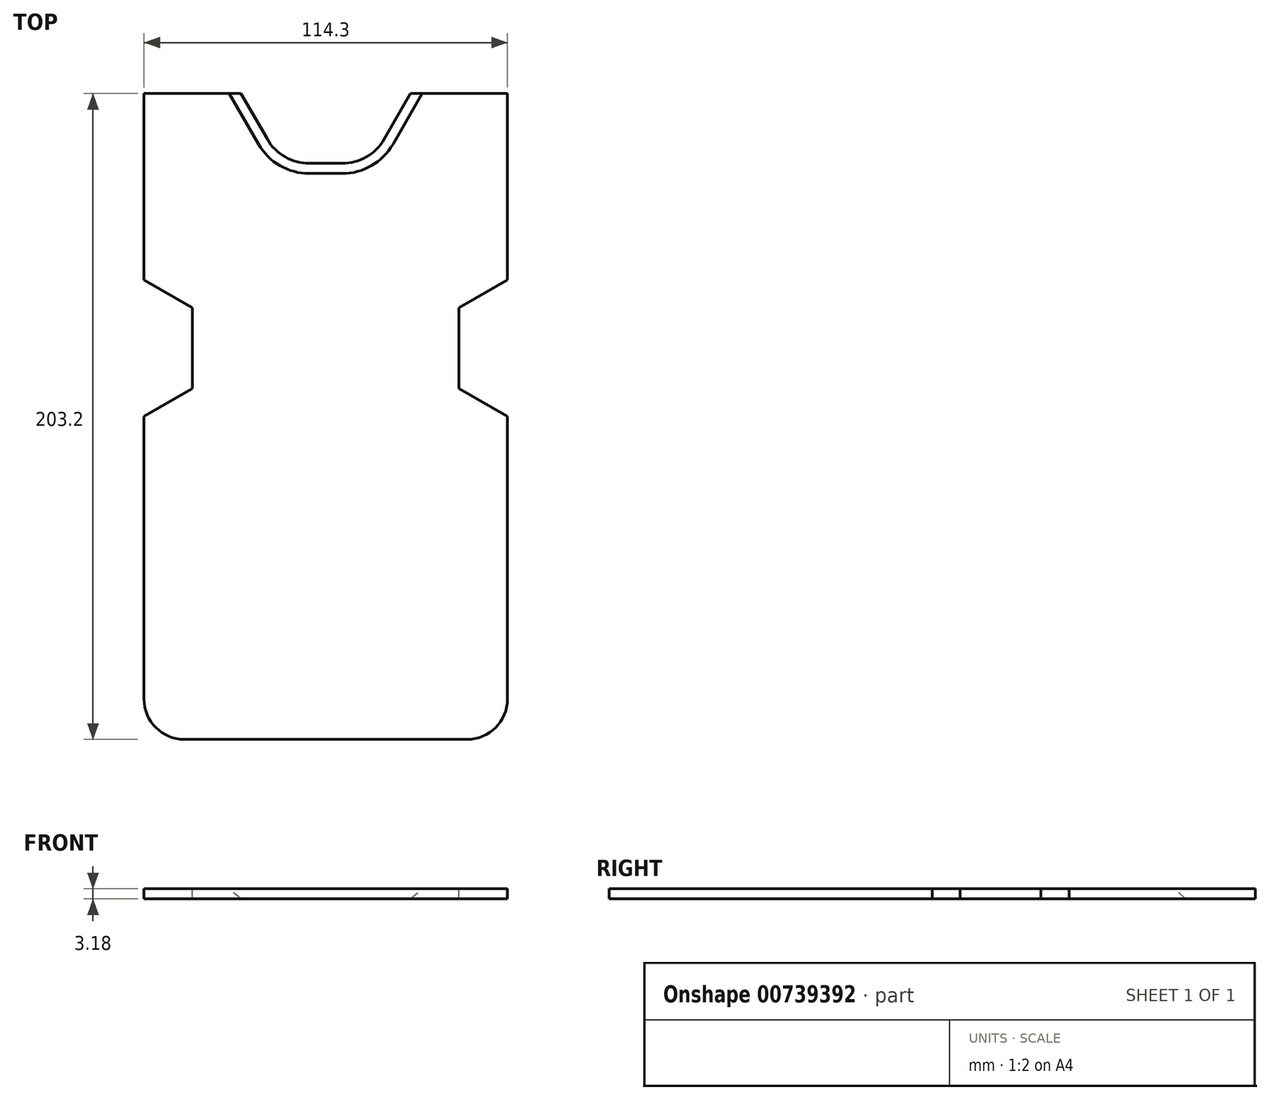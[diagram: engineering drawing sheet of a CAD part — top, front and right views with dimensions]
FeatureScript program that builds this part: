
annotation { "Feature Type Name" : "Feature", "Feature Type Description" : "" }
export const myFeature = defineFeature(function(context is Context, id is Id, definition is map)
    precondition{}
    {
        {
            var Q0;
            Q0=qCreatedBy(makeId("Top.planeOp"),FACE);
            var sketch = newSketch(context, id + "F0", { "sketchPlane" : qUnion([Q0])});
            skLineSegment(sketch, "E0.bottom", {"start": v(-57.15, -25.4) * mm, "end": v(57.15, -25.4) * mm});
            skLineSegment(sketch, "E0.top", {"start": v(-57.15, 25.4) * mm, "end": v(57.15, 25.4) * mm});
            skLineSegment(sketch, "E0.left", {"start": v(-57.15, -25.4) * mm, "end": v(-57.15, 25.4) * mm});
            skLineSegment(sketch, "E0.right", {"start": v(57.15, -25.4) * mm, "end": v(57.15, 25.4) * mm});
            skLineSegment(sketch, "E1", {"start": v(57.15, -25.4) * mm, "end": v(-57.15, 25.4) * mm, "construction": true});
            skLineSegment(sketch, "E2", {"start": v(57.15, 25.4) * mm, "end": v(-57.15, -25.4) * mm, "construction": true});
            skPoint(sketch, "E3", {"position": v(0, 0) * mm});
            skSolve(sketch);
        }
        {
            var Q0;
            Q0=makeQuery(id+"F0.imprint","IMPRINT",FACE,{"disambiguationData":[TD([[makeQuery(id+"F0.imprint","IMPRINT",EDGE,{"derivedFrom":sQuery(id+"F0.wireOp",EDGE,"E0.bottom")}),1.0]])]});
            extrude(context, id + "F1", {"entities" : qUnion([Q0]), "depth" : 3.17 * mm, "offsetDistance" : 25.4 * mm});
        }
        {
            var Q0;
            Q0=makeQuery(id+"F1.opExtrude","SWEPT_FACE",FACE,{"disambiguationData":[OSD([sQuery(id+"F0.wireOp",EDGE,"E0.top")])]});
            extrude(context, id + "F2", {"entities" : qUnion([Q0]), "operationType" : NewBodyOperationType.ADD, "depth" : 152.4 * mm, "offsetDistance" : 25.4 * mm});
        }
        {
            var Q0;
            {var subQ0=sQuery(id+"F0.wireOp",EDGE,"E0.top");Q0=makeQuery(id+"F2.boolean.opBoolean","MERGE",FACE,{"derivedFrom":[makeQuery(id+"F1.opExtrude","CAP_FACE",FACE,{"disambiguationData":[OSD([sQuery(id+"F0.wireOp",EDGE,"E0.bottom"),subQ0,sQuery(id+"F0.wireOp",EDGE,"E0.left"),sQuery(id+"F0.wireOp",EDGE,"E0.right")])],"isStart":false}),makeQuery(id+"F2.opExtrude","SWEPT_FACE",FACE,{"disambiguationData":[OSD([subQ0]),TDD([makeQuery(id+"F1.opExtrude","CAP_EDGE",EDGE,{"disambiguationData":[OSD([subQ0])],"isStart":false})])]})]});}
            var sketch = newSketch(context, id + "F3", { "sketchPlane" : qUnion([Q0])});
            skLineSegment(sketch, "E4", {"start": v(13.97, 155.8) * mm, "end": v(-13.97, 155.8) * mm});
            skLineSegment(sketch, "E5", {"start": v(-13.97, 155.8) * mm, "end": v(-26.67, 177.8) * mm});
            skLineSegment(sketch, "E6", {"start": v(13.97, 155.8) * mm, "end": v(26.67, 177.8) * mm});
            skLineSegment(sketch, "E7", {"start": v(0, 155.8) * mm, "end": v(0, 177.8) * mm, "construction": true});
            skLineSegment(sketch, "E8", {"start": v(-57.15, 76.2) * mm, "end": v(-41.91, 85) * mm});
            skLineSegment(sketch, "E9", {"start": v(-41.91, 85) * mm, "end": v(-41.91, 110.4) * mm});
            skLineSegment(sketch, "E10", {"start": v(-41.9, 110.4) * mm, "end": v(-57.15, 119.2) * mm});
            skLineSegment(sketch, "E11", {"start": v(57.15, 76.2) * mm, "end": v(41.91, 85) * mm});
            skLineSegment(sketch, "E12", {"start": v(41.91, 85) * mm, "end": v(41.91, 110.4) * mm});
            skLineSegment(sketch, "E13", {"start": v(41.91, 110.4) * mm, "end": v(57.15, 119.2) * mm});
            skSolve(sketch);
        }
        {
            var Q0;
            Q0=makeQuery(id+"F3.imprint","IMPRINT",FACE,{"disambiguationData":[TD([[makeQuery(id+"F3.imprint","IMPRINT",EDGE,{"derivedFrom":sQuery(id+"F3.wireOp",EDGE,"E4")}),-1.0]])]});
            extrude(context, id + "F4", {"entities" : qUnion([Q0]), "operationType" : NewBodyOperationType.REMOVE, "oppositeDirection" : true, "depth" : 3.3 * mm, "offsetDistance" : 25.4 * mm});
        }
        {
            var Q0;
            Q0=makeQuery(id+"F4.boolean.opBoolean","COPY",EDGE,{"derivedFrom":makeQuery(id+"F4.opExtrude","SWEPT_EDGE",EDGE,{"disambiguationData":[OSD([sQuery(id+"F3.wireOp",EDGE,"E4"),sQuery(id+"F3.wireOp",EDGE,"E6")])]})});
            var Q1;
            Q1=makeQuery(id+"F4.boolean.opBoolean","COPY",EDGE,{"derivedFrom":makeQuery(id+"F4.opExtrude","SWEPT_EDGE",EDGE,{"disambiguationData":[OSD([sQuery(id+"F3.wireOp",EDGE,"E4"),sQuery(id+"F3.wireOp",EDGE,"E5")])]})});
            fillet(context, id + "F5", {"entities" : qUnion([Q0, Q1]), "radius" : 15.24 * mm, "tangentPropagation" : true, "allowEdgeOverflow" : false});
        }
        {
            var Q0;
            Q0=makeQuery(id+"F1.opExtrude","SWEPT_EDGE",EDGE,{"disambiguationData":[OSD([sQuery(id+"F0.wireOp",EDGE,"E0.bottom"),sQuery(id+"F0.wireOp",EDGE,"E0.right")])]});
            var Q1;
            Q1=makeQuery(id+"F1.opExtrude","SWEPT_EDGE",EDGE,{"disambiguationData":[OSD([sQuery(id+"F0.wireOp",EDGE,"E0.bottom"),sQuery(id+"F0.wireOp",EDGE,"E0.left")])]});
            fillet(context, id + "F6", {"entities" : qUnion([Q0, Q1]), "radius" : 12.7 * mm, "tangentPropagation" : true, "allowEdgeOverflow" : false});
        }
        {
            var Q0;
            {var subQ0=sQuery(id+"F3.wireOp",EDGE,"E11");Q0=makeQuery(id+"F3.imprint","IMPRINT",FACE,{"disambiguationData":[TD([[makeQuery(id+"F3.imprint","IMPRINT",EDGE,{"derivedFrom":subQ0}),-1.0]])]});}
            var Q1;
            {var subQ0=sQuery(id+"F3.wireOp",EDGE,"E8");Q1=makeQuery(id+"F3.imprint","IMPRINT",FACE,{"disambiguationData":[TD([[makeQuery(id+"F3.imprint","IMPRINT",EDGE,{"derivedFrom":subQ0}),1.0]])]});}
            extrude(context, id + "F7", {"entities" : qUnion([Q0, Q1]), "operationType" : NewBodyOperationType.REMOVE, "oppositeDirection" : true, "depth" : 3.17 * mm, "offsetDistance" : 25.4 * mm});
        }
        {
            var Q0;
            Q0=makeQuery(id+"F4.boolean.opBoolean","COPY",EDGE,{"derivedFrom":makeQuery(id+"F4.opExtrude","CAP_EDGE",EDGE,{"disambiguationData":[OSD([sQuery(id+"F3.wireOp",EDGE,"E5")])],"isStart":true})});
            var Q1;
            {var subQ0=sQuery(id+"F0.wireOp",EDGE,"E0.top");Q1=makeQuery(id+"F5.opFillet","BLEND_EDGE",EDGE,{"blendedFrom":[makeQuery(id+"F4.boolean.opBoolean","COPY",EDGE,{"derivedFrom":makeQuery(id+"F4.opExtrude","SWEPT_EDGE",EDGE,{"disambiguationData":[OSD([sQuery(id+"F3.wireOp",EDGE,"E4"),sQuery(id+"F3.wireOp",EDGE,"E5")])]})}),makeQuery(id+"F2.boolean.opBoolean","MERGE",FACE,{"derivedFrom":[makeQuery(id+"F1.opExtrude","CAP_FACE",FACE,{"disambiguationData":[OSD([sQuery(id+"F0.wireOp",EDGE,"E0.bottom"),subQ0,sQuery(id+"F0.wireOp",EDGE,"E0.left"),sQuery(id+"F0.wireOp",EDGE,"E0.right")])],"isStart":false}),makeQuery(id+"F2.opExtrude","SWEPT_FACE",FACE,{"disambiguationData":[OSD([subQ0]),TDD([makeQuery(id+"F1.opExtrude","CAP_EDGE",EDGE,{"disambiguationData":[OSD([subQ0])],"isStart":false})])]})]})],"blendedInto":[makeQuery(id+"F2.boolean.opBoolean","MERGE",FACE,{"derivedFrom":[makeQuery(id+"F1.opExtrude","CAP_FACE",FACE,{"disambiguationData":[OSD([sQuery(id+"F0.wireOp",EDGE,"E0.bottom"),subQ0,sQuery(id+"F0.wireOp",EDGE,"E0.left"),sQuery(id+"F0.wireOp",EDGE,"E0.right")])],"isStart":false}),makeQuery(id+"F2.opExtrude","SWEPT_FACE",FACE,{"disambiguationData":[OSD([subQ0]),TDD([makeQuery(id+"F1.opExtrude","CAP_EDGE",EDGE,{"disambiguationData":[OSD([subQ0])],"isStart":false})])]})]})]});}
            var Q2;
            Q2=makeQuery(id+"F4.boolean.opBoolean","COPY",EDGE,{"derivedFrom":makeQuery(id+"F4.opExtrude","CAP_EDGE",EDGE,{"disambiguationData":[OSD([sQuery(id+"F3.wireOp",EDGE,"E4")])],"isStart":true})});
            var Q3;
            {var subQ0=sQuery(id+"F0.wireOp",EDGE,"E0.top");Q3=makeQuery(id+"F5.opFillet","BLEND_EDGE",EDGE,{"blendedFrom":[makeQuery(id+"F4.boolean.opBoolean","COPY",EDGE,{"derivedFrom":makeQuery(id+"F4.opExtrude","SWEPT_EDGE",EDGE,{"disambiguationData":[OSD([sQuery(id+"F3.wireOp",EDGE,"E4"),sQuery(id+"F3.wireOp",EDGE,"E6")])]})}),makeQuery(id+"F2.boolean.opBoolean","MERGE",FACE,{"derivedFrom":[makeQuery(id+"F1.opExtrude","CAP_FACE",FACE,{"disambiguationData":[OSD([sQuery(id+"F0.wireOp",EDGE,"E0.bottom"),subQ0,sQuery(id+"F0.wireOp",EDGE,"E0.left"),sQuery(id+"F0.wireOp",EDGE,"E0.right")])],"isStart":false}),makeQuery(id+"F2.opExtrude","SWEPT_FACE",FACE,{"disambiguationData":[OSD([subQ0]),TDD([makeQuery(id+"F1.opExtrude","CAP_EDGE",EDGE,{"disambiguationData":[OSD([subQ0])],"isStart":false})])]})]})],"blendedInto":[makeQuery(id+"F2.boolean.opBoolean","MERGE",FACE,{"derivedFrom":[makeQuery(id+"F1.opExtrude","CAP_FACE",FACE,{"disambiguationData":[OSD([sQuery(id+"F0.wireOp",EDGE,"E0.bottom"),subQ0,sQuery(id+"F0.wireOp",EDGE,"E0.left"),sQuery(id+"F0.wireOp",EDGE,"E0.right")])],"isStart":false}),makeQuery(id+"F2.opExtrude","SWEPT_FACE",FACE,{"disambiguationData":[OSD([subQ0]),TDD([makeQuery(id+"F1.opExtrude","CAP_EDGE",EDGE,{"disambiguationData":[OSD([subQ0])],"isStart":false})])]})]})]});}
            var Q4;
            Q4=makeQuery(id+"F4.boolean.opBoolean","COPY",EDGE,{"derivedFrom":makeQuery(id+"F4.opExtrude","CAP_EDGE",EDGE,{"disambiguationData":[OSD([sQuery(id+"F3.wireOp",EDGE,"E6")])],"isStart":true})});
            chamfer(context, id + "F8", {"entities" : qUnion([Q0, Q1, Q2, Q3, Q4]), "width" : 3.17 * mm, "tangentPropagation" : true});
        }
    });
